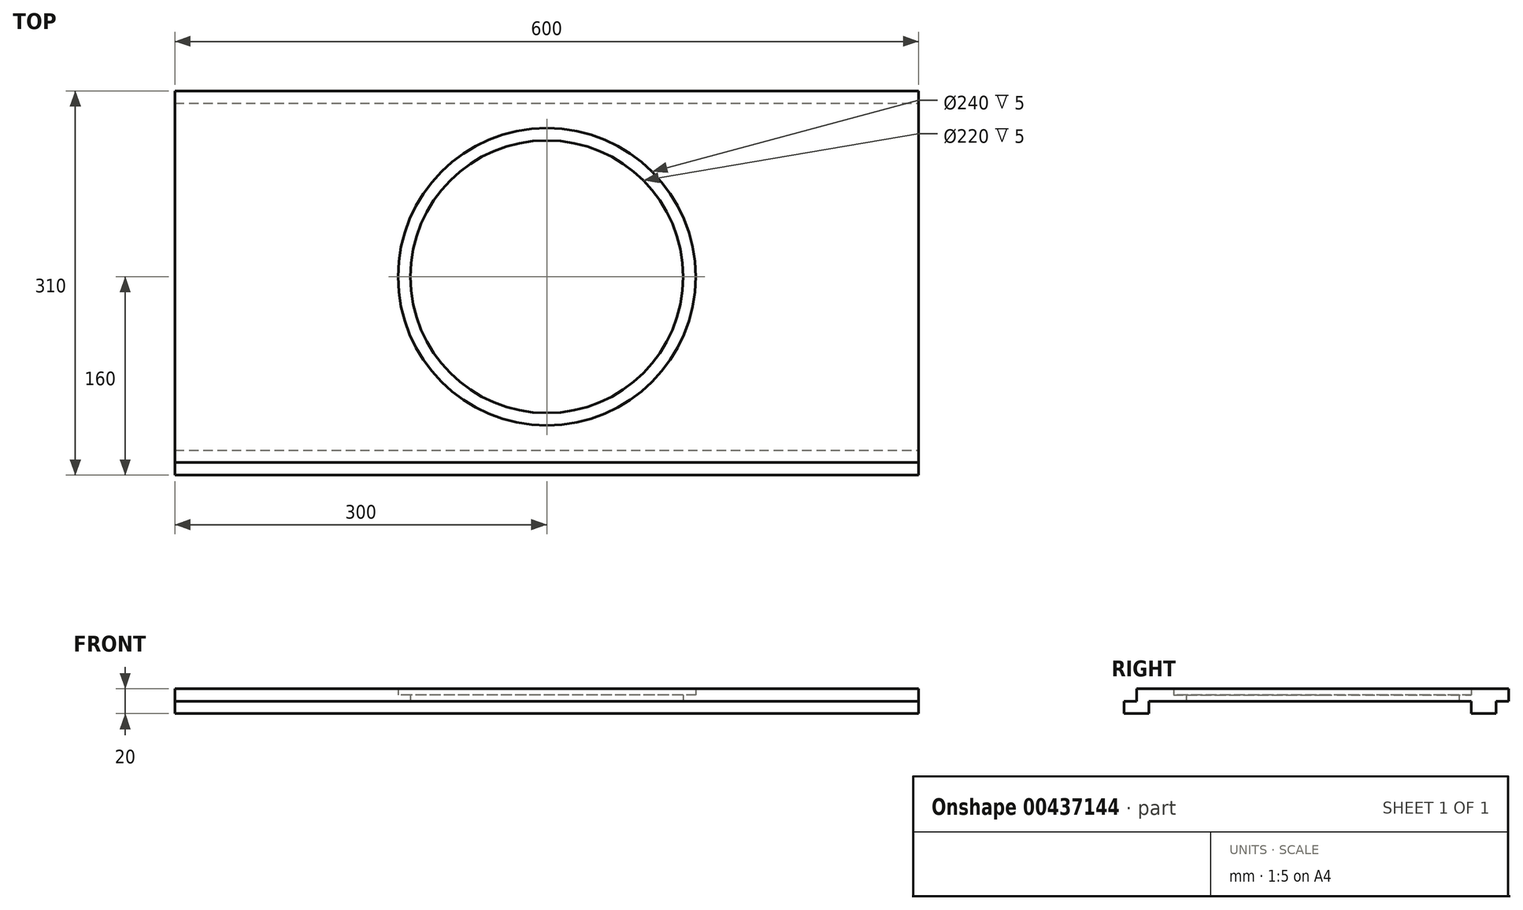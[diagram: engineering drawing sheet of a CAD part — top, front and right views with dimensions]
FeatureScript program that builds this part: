
annotation { "Feature Type Name" : "Feature", "Feature Type Description" : "" }
export const myFeature = defineFeature(function(context is Context, id is Id, definition is map)
    precondition{}
    {
        {
            var Q0;
            Q0=qCreatedBy(makeId("Top.planeOp"),FACE);
            var sketch = newSketch(context, id + "F0", { "sketchPlane" : qUnion([Q0])});
            skLineSegment(sketch, "E0.bottom", {"start": v(300, 150) * mm, "end": v(-300, 150) * mm});
            skLineSegment(sketch, "E0.top", {"start": v(300, -150) * mm, "end": v(-300, -150) * mm});
            skLineSegment(sketch, "E0.left", {"start": v(300, 150) * mm, "end": v(300, -150) * mm});
            skLineSegment(sketch, "E0.right", {"start": v(-300, 150) * mm, "end": v(-300, -150) * mm});
            skPoint(sketch, "E0.middle", {"position": v(0, 0) * mm});
            skLineSegment(sketch, "E1", {"start": v(-300, 0) * mm, "end": v(300, 0) * mm, "construction": true});
            skCircle(sketch, "E2", {"center": v(0, 0) * mm, "radius": 120 * mm});
            skCircle(sketch, "E3", {"center": v(0, 0) * mm, "radius": 110 * mm});
            skSolve(sketch);
        }
        {
            var Q0;
            Q0=makeQuery(id+"F0.imprint","IMPRINT",FACE,{"disambiguationData":[TD([[makeQuery(id+"F0.imprint","IMPRINT",EDGE,{"derivedFrom":sQuery(id+"F0.wireOp",EDGE,"E0.bottom")}),1.0]])]});
            extrude(context, id + "F1", {"entities" : qUnion([Q0]), "depth" : 10 * mm});
        }
        {
            var Q0;
            Q0=makeQuery(id+"F0.imprint","IMPRINT",FACE,{"disambiguationData":[TD([[makeQuery(id+"F0.imprint","IMPRINT",EDGE,{"derivedFrom":sQuery(id+"F0.wireOp",EDGE,"E2")}),1.0]])]});
            var Q1;
            Q1=makeQuery(id+"F0.imprint","IMPRINT",FACE,{"disambiguationData":[TD([[makeQuery(id+"F0.imprint","IMPRINT",EDGE,{"derivedFrom":sQuery(id+"F0.wireOp",EDGE,"h54LD8P5-nfIt-8PUf-szoY-WRV6JTvWVeSX")}),1.0]])]});
            extrude(context, id + "F2", {"entities" : qUnion([Q0, Q1]), "operationType" : NewBodyOperationType.ADD, "depth" : 5 * mm});
        }
        {
            var Q0;
            Q0=makeQuery(id+"F0.imprint","IMPRINT",FACE,{"disambiguationData":[TD([[makeQuery(id+"F0.imprint","IMPRINT",EDGE,{"derivedFrom":sQuery(id+"F0.wireOp",EDGE,"E0.bottom")}),1.0]])]});
            var sketch = newSketch(context, id + "F3", { "sketchPlane" : qUnion([Q0])});
            skLineSegment(sketch, "E4.0", {"start": v(-300, 150) * mm, "end": v(-300, -150) * mm, "construction": true});
            skLineSegment(sketch, "E5.0", {"start": v(300, 150) * mm, "end": v(300, -150) * mm, "construction": true});
            skLineSegment(sketch, "E6.0", {"start": v(300, -150) * mm, "end": v(-300, -150) * mm, "construction": true});
            skLineSegment(sketch, "E7.0", {"start": v(300, 150) * mm, "end": v(-300, 150) * mm, "construction": true});
            skLineSegment(sketch, "E8.bottom", {"start": v(-300, 140) * mm, "end": v(300, 140) * mm});
            skLineSegment(sketch, "E8.top", {"start": v(-300, 120) * mm, "end": v(300, 120) * mm});
            skLineSegment(sketch, "E8.left", {"start": v(-300, 140) * mm, "end": v(-300, 120) * mm});
            skLineSegment(sketch, "E8.right", {"start": v(300, 140) * mm, "end": v(300, 120) * mm});
            skLineSegment(sketch, "E9.bottom", {"start": v(-300, -140) * mm, "end": v(300, -140) * mm});
            skLineSegment(sketch, "E9.top", {"start": v(-300, -160) * mm, "end": v(300, -160) * mm});
            skLineSegment(sketch, "E9.left", {"start": v(-300, -140) * mm, "end": v(-300, -160) * mm});
            skLineSegment(sketch, "E9.right", {"start": v(300, -140) * mm, "end": v(300, -160) * mm});
            skSolve(sketch);
        }
        {
            var Q0;
            {var subQ0=sQuery(id+"F3.wireOp",EDGE,"E9.bottom");Q0=makeQuery(id+"F3.imprint","IMPRINT",FACE,{"disambiguationData":[TD([[makeQuery(id+"F3.imprint","IMPRINT",EDGE,{"derivedFrom":subQ0}),-1.0]])]});}
            var Q1;
            {var subQ0=sQuery(id+"F3.wireOp",EDGE,"E9.top");Q1=makeQuery(id+"F3.imprint","IMPRINT",FACE,{"disambiguationData":[TD([[makeQuery(id+"F3.imprint","IMPRINT",EDGE,{"derivedFrom":subQ0}),1.0]])]});}
            var Q2;
            Q2=makeQuery(id+"F3.imprint","IMPRINT",FACE,{"disambiguationData":[TD([[makeQuery(id+"F3.imprint","IMPRINT",EDGE,{"derivedFrom":sQuery(id+"F3.wireOp",EDGE,"E8.bottom")}),-1.0]])]});
            extrude(context, id + "F4", {"entities" : qUnion([Q0, Q1, Q2]), "operationType" : NewBodyOperationType.ADD, "oppositeDirection" : true, "depth" : 10 * mm});
        }
    });
